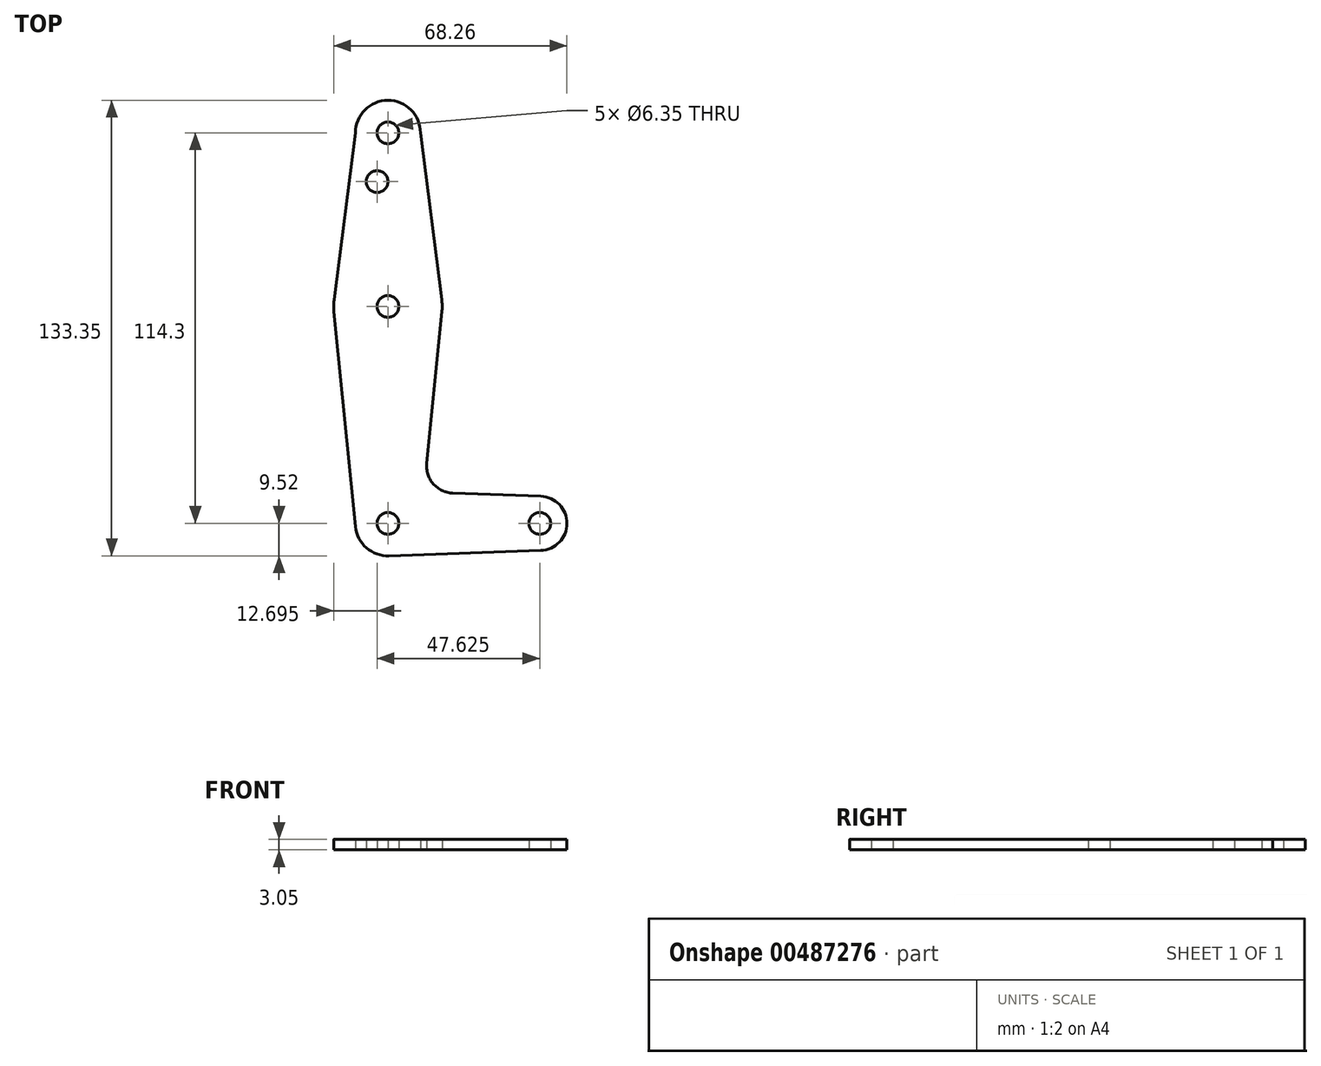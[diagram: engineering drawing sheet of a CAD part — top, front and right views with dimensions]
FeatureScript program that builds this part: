
annotation { "Feature Type Name" : "Feature", "Feature Type Description" : "" }
export const myFeature = defineFeature(function(context is Context, id is Id, definition is map)
    precondition{}
    {
        {
            var Q0;
            Q0=qCreatedBy(makeId("Top.planeOp"),FACE);
            var sketch = newSketch(context, id + "F0", { "sketchPlane" : qUnion([Q0])});
            skLineSegment(sketch, "E0", {"start": v(0, 0) * mm, "end": v(0, 114.3) * mm, "construction": true});
            skLineSegment(sketch, "E1", {"start": v(0, 0) * mm, "end": v(44.45, 0) * mm, "construction": true});
            skCircle(sketch, "E2", {"center": v(0, 114.3) * mm, "radius": 9.53 * mm});
            skCircle(sketch, "E3", {"center": v(0, 0) * mm, "radius": 9.53 * mm});
            skCircle(sketch, "E4", {"center": v(44.45, 0) * mm, "radius": 7.94 * mm});
            skCircle(sketch, "E5", {"center": v(0, 63.5) * mm, "radius": 15.88 * mm});
            skLineSegment(sketch, "E6", {"start": v(9.53, 114.3) * mm, "end": v(15.75, 65.5) * mm});
            skLineSegment(sketch, "E7", {"start": v(-9.53, 114.3) * mm, "end": v(-15.75, 65.5) * mm});
            skLineSegment(sketch, "E8", {"start": v(15.8, 61.91) * mm, "end": v(11.34, 17.6) * mm});
            skLineSegment(sketch, "E9", {"start": v(-9.48, -0.95) * mm, "end": v(-15.8, 61.91) * mm});
            skLineSegment(sketch, "E10", {"start": v(44.73, 7.93) * mm, "end": v(18.97, 8.85) * mm});
            skLineSegment(sketch, "E11", {"start": v(44.73, -7.93) * mm, "end": v(0.34, -9.52) * mm});
            skCircle(sketch, "E12", {"center": v(0, 114.3) * mm, "radius": 3.18 * mm});
            skCircle(sketch, "E13", {"center": v(0, 63.5) * mm, "radius": 3.18 * mm});
            skCircle(sketch, "E14", {"center": v(0, 0) * mm, "radius": 3.18 * mm});
            skCircle(sketch, "E15", {"center": v(44.45, 0) * mm, "radius": 3.18 * mm});
            skCircle(sketch, "E16", {"center": v(-3.18, 100.03) * mm, "radius": 3.18 * mm});
            skArc(sketch, "E17.filletArc", {"start": v(11.34, 17.6) * mm, "mid": v(13.26, 11.57) * mm, "end": v(18.97, 8.85) * mm});
            skSolve(sketch);
        }
        {
            var Q0;
            Q0 = qSketchRegion(id + "F0", true);
            extrude(context, id + "F1", {"entities" : qUnion([Q0]), "depth" : 3.05 * mm});
        }
    });
